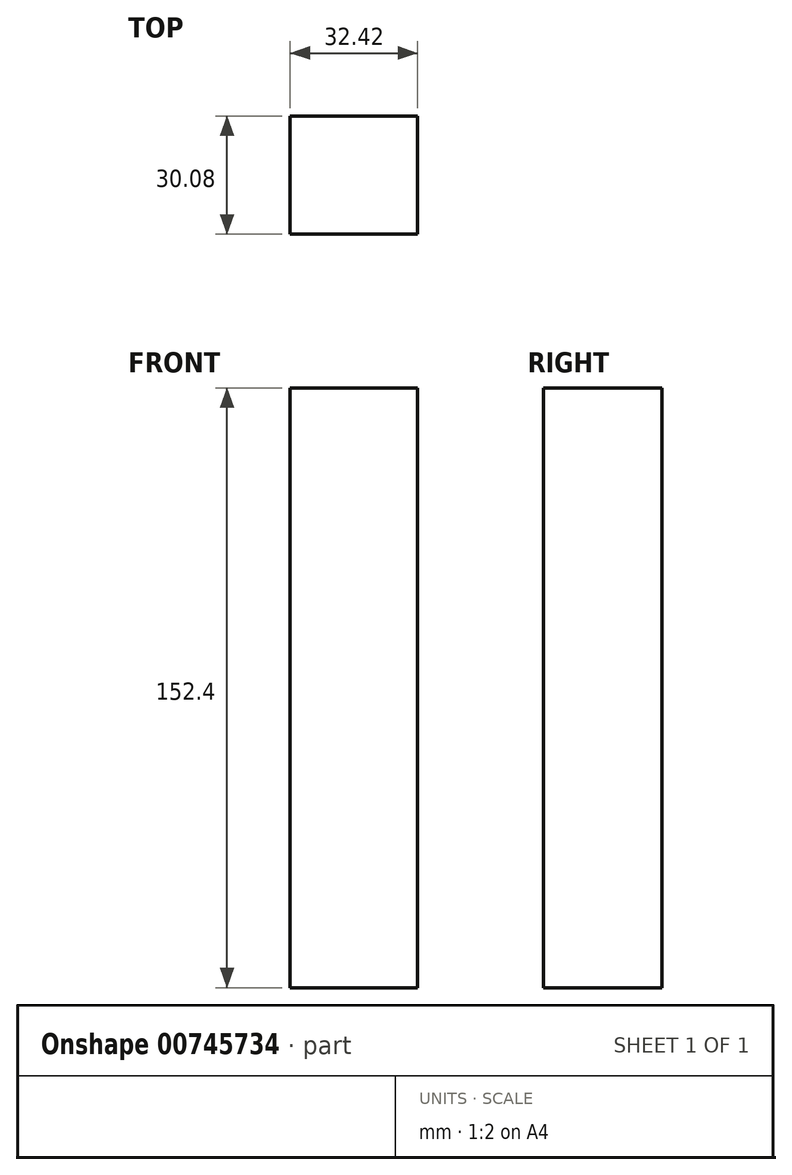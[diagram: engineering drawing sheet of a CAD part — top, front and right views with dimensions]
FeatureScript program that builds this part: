
annotation { "Feature Type Name" : "Feature", "Feature Type Description" : "" }
export const myFeature = defineFeature(function(context is Context, id is Id, definition is map)
    precondition{}
    {
        {
            var Q0;
            Q0=qCreatedBy(makeId("Top.planeOp"),FACE);
            var sketch = newSketch(context, id + "F0", { "sketchPlane" : qUnion([Q0])});
            skLineSegment(sketch, "E0.bottom", {"start": v(16.2, 15.04) * mm, "end": v(-16.2, 15.04) * mm});
            skLineSegment(sketch, "E0.top", {"start": v(16.2, -15.04) * mm, "end": v(-16.2, -15.04) * mm});
            skLineSegment(sketch, "E0.left", {"start": v(16.2, 15.04) * mm, "end": v(16.2, -15.04) * mm});
            skLineSegment(sketch, "E0.right", {"start": v(-16.2, 15.04) * mm, "end": v(-16.2, -15.04) * mm});
            skPoint(sketch, "E0.middle", {"position": v(0, 0) * mm});
            skSolve(sketch);
        }
        {
            var Q0;
            Q0=makeQuery(id+"F0.imprint","IMPRINT",FACE,{"disambiguationData":[TD([[makeQuery(id+"F0.imprint","IMPRINT",EDGE,{"derivedFrom":sQuery(id+"F0.wireOp",EDGE,"E0.bottom")}),1.0]])]});
            extrude(context, id + "F1", {"entities" : qUnion([Q0]), "depth" : 152.4 * mm, "offsetDistance" : 25.4 * mm});
        }
    });
